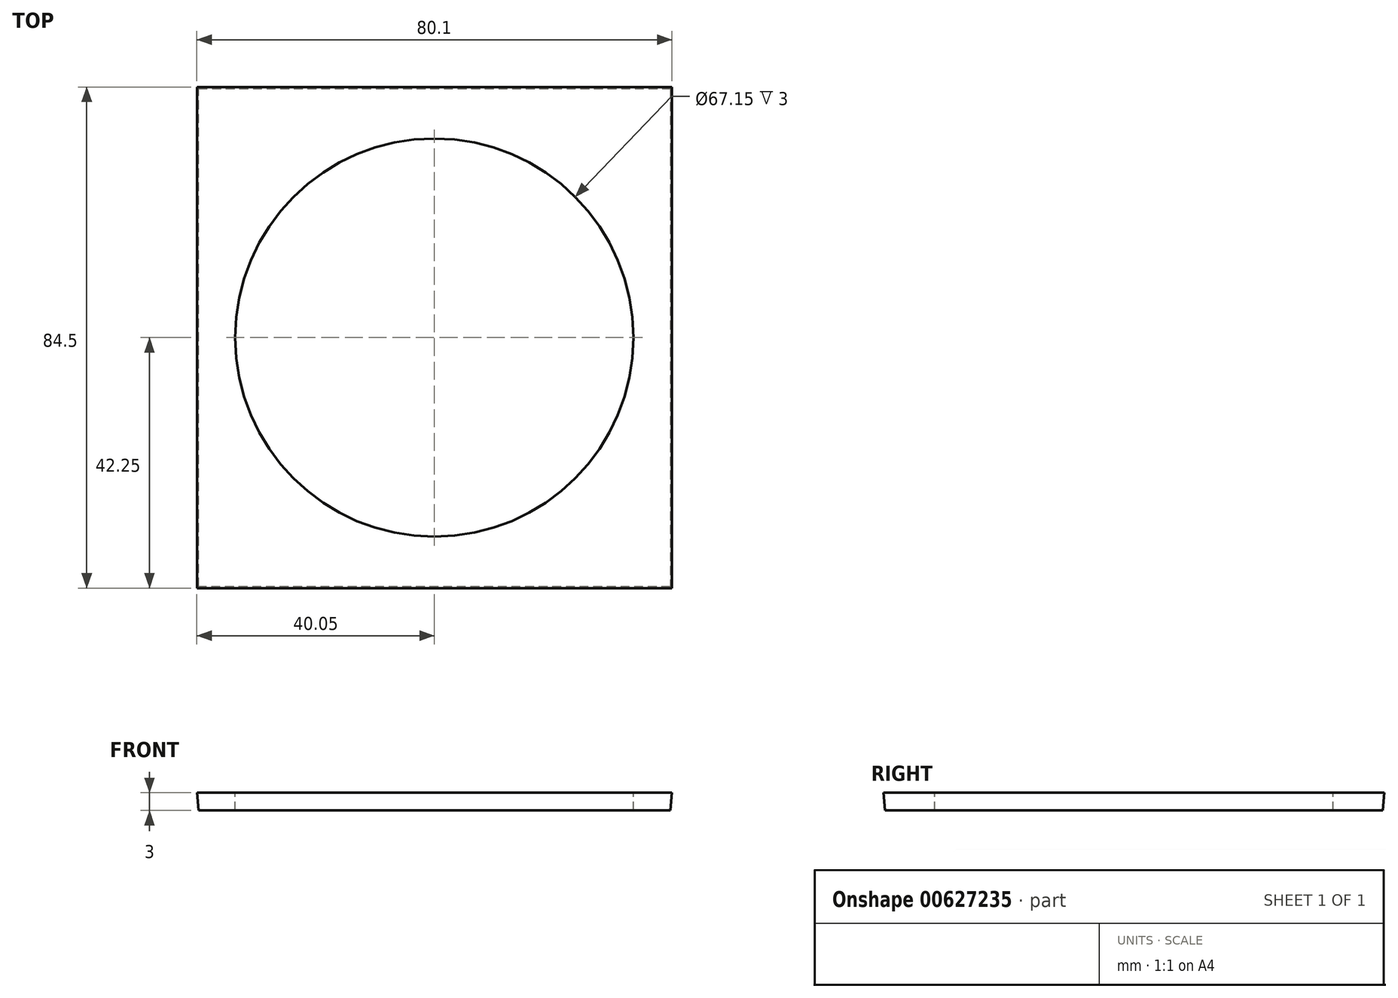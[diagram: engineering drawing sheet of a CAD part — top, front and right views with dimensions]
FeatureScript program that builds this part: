
annotation { "Feature Type Name" : "Feature", "Feature Type Description" : "" }
export const myFeature = defineFeature(function(context is Context, id is Id, definition is map)
    precondition{}
    {
        {
            var Q0;
            Q0=qCreatedBy(makeId("Top.planeOp"),FACE);
            var sketch = newSketch(context, id + "F0", { "sketchPlane" : qUnion([Q0])});
            skLineSegment(sketch, "E0.bottom", {"start": v(-39.78, 41.99) * mm, "end": v(39.78, 41.99) * mm});
            skLineSegment(sketch, "E0.top", {"start": v(-39.78, -41.99) * mm, "end": v(39.78, -41.99) * mm});
            skLineSegment(sketch, "E0.left", {"start": v(-39.78, 41.99) * mm, "end": v(-39.78, -41.99) * mm});
            skLineSegment(sketch, "E0.right", {"start": v(39.78, 41.99) * mm, "end": v(39.78, -41.99) * mm});
            skPoint(sketch, "E0.middle", {"position": v(0, 0) * mm});
            skSolve(sketch);
        }
        {
            var Q0;
            Q0=makeQuery(id+"F0.imprint","IMPRINT",FACE,{"disambiguationData":[TD([[makeQuery(id+"F0.imprint","IMPRINT",EDGE,{"derivedFrom":sQuery(id+"F0.wireOp",EDGE,"E0.bottom")}),-1.0]])]});
            extrude(context, id + "F1", {"entities" : qUnion([Q0]), "depth" : 3 * mm, "offsetDistance" : 25.4 * mm, "hasDraft" : true, "draftAngle" : 5 * degree});
        }
        {
            var Q0;
            Q0=makeQuery(id+"F1.opExtrude","CAP_FACE",FACE,{"disambiguationData":[OSD([sQuery(id+"F0.wireOp",EDGE,"E0.bottom"),sQuery(id+"F0.wireOp",EDGE,"E0.top"),sQuery(id+"F0.wireOp",EDGE,"E0.left"),sQuery(id+"F0.wireOp",EDGE,"E0.right")])],"isStart":false});
            var sketch = newSketch(context, id + "F2", { "sketchPlane" : qUnion([Q0])});
            skCircle(sketch, "E1", {"center": v(0, 0) * mm, "radius": 33.58 * mm});
            skSolve(sketch);
        }
        {
            var Q0;
            Q0=makeQuery(id+"F2.imprint","IMPRINT",FACE,{"disambiguationData":[TD([[makeQuery(id+"F2.imprint","IMPRINT",EDGE,{"derivedFrom":sQuery(id+"F2.wireOp",EDGE,"E1")}),1.0]])]});
            extrude(context, id + "F3", {"entities" : qUnion([Q0]), "operationType" : NewBodyOperationType.REMOVE, "oppositeDirection" : true, "depth" : 80 * mm, "offsetDistance" : 25.4 * mm});
        }
        {
            var Q0;
            Q0=makeQuery(id+"F1.opExtrude","SWEPT_FACE",FACE,{"disambiguationData":[OSD([sQuery(id+"F0.wireOp",EDGE,"E0.top")])]});
            var sketch = newSketch(context, id + "F4", { "sketchPlane" : qUnion([Q0])});
            skText(sketch, "E2", { "text": "Leothek", "fontName": "OpenSans-Italic.ttf"});
            skPoint(sketch, "E2.firstSnap0", {"position": v(0, 6.67) * mm});
            const initialGuessF4  = {"E2": [-0.03756, 0.02226, 1, 0, 0.00772]};
            skSetInitialGuess(sketch, initialGuessF4);
            skSolve(sketch);
        }
        {
            var Q0;
            Q0 = qSketchRegion(id + "F4", true);
            extrude(context, id + "F5", {"entities" : qUnion([Q0]), "operationType" : NewBodyOperationType.REMOVE, "oppositeDirection" : true, "depth" : 5 * mm, "offsetDistance" : 25.4 * mm});
        }
    });
